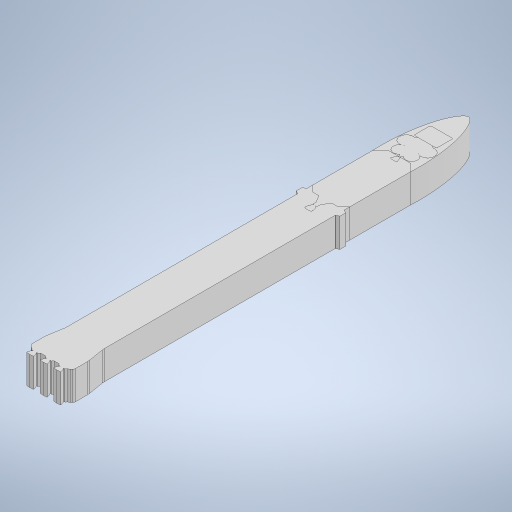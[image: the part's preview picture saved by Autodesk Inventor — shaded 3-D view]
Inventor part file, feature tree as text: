
AUTODESK INVENTOR PART (.ipt)
format: ipt  version: 2024.1 (Build 281209000, 209)  size: 606,208 bytes
history: native  units: mm
features: extrude x5, chamfer x5, fillet x2, sketch x1
ambient origin geometry x8: Origin, YZ Plane, XZ Plane, XY Plane, X Axis, Y Axis, Z Axis, Center Point
bodies: Solid1 (feature_tree), Solid2 (feature_tree), Solid3 (feature_tree), Solid4 (feature_tree), Solid5 (feature_tree)
feature tree (13):
  sketch  "Sketch1"  dims[d0=83.7mm d1=13.0mm d2=6.5mm d3=41.85mm d4=3.0mm d5=1.1mm d6=1.1mm d7=12.0mm d8=15.0mm d9=23.0mm d10=1.0mm d11=1.0mm d12=27.0mm d13=3.0mm d14=3.0mm d15=3.0mm d16=1.3mm d17=1.3mm d18=1.7mm d19=1.7mm d20=8.726646mm d21=8.726646mm d22=2.13751mm d24=2.13751mm d26=8.726646mm d28=8.726646mm d29=30.0mm d31=4.7mm d32=10.0mm d34=10.0mm d36=6.0mm d37=10.0mm d38=0.0mm d39=0.5mm d40=1.0mm d41=45.0deg d42=0.5mm d43=1.0mm d44=45.0deg d45=0.5mm d46=1.0mm d47=45.0deg d48=0.5mm d49=1.0mm d50=45.0deg d57=2.2mm d58=2.2mm d59=3.7mm d60=3.7mm d61=0.35mm d62=0.35mm d63=1.4mm d64=1.4mm d65=3.5mm d66=3.5mm d67=0.7mm d68=10.0mm d69=0.0mm d70=10.0mm d71=0.0mm d72=0.3mm d73=0.3mm d74=0.3mm d75=0.3mm d76=0.3mm d77=0.3mm d78=0.3mm d79=0.3mm d80=10.0mm d81=0.0mm d82=0.3mm d83=10.0mm d84=0.0mm d85=1.0mm d86=1.0mm d87=45.0deg d88=1.0mm d89=4.0mm d90=2.0mm d91=2.0mm d92=2.0mm d93=2.0mm]
  extrude  "Extrusion1"  Depth=4.0mm
  extrude  "Extrusion2"  Depth=4.0mm
  extrude  "Extrusion3"  Depth=4.0mm
  extrude  "Extrusion4"  Depth=4.0mm
  extrude  "Extrusion5"  Depth=4.0mm
  chamfer  "Chamfer1"  Distance=1.1mm
  chamfer  "Chamfer2"  Distance=12.0mm
  chamfer  "Chamfer3"  Distance=15.0mm
  chamfer  "Chamfer4"  Distance=23.0mm
  chamfer  "Chamfer5"  Distance=1.0mm
  fillet  "Fillet1"  Radius=1.0mm
  fillet  "Fillet2"  Radius=27.0mm
